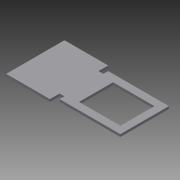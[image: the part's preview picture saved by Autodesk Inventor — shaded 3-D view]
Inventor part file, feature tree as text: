
AUTODESK INVENTOR PART (.ipt)
format: ipt  version: 2014 (Build 180170000, 170)  size: 101,376 bytes
history: native  units: mm
features: extrude x2, sketch x2
ambient origin geometry x8: Origin, YZ Plane, XZ Plane, XY Plane, X Axis, Y Axis, Z Axis, Center Point
bodies: Volumenkörper1 (feature_tree)
feature tree (4):
  extrude  "Extrusion1"  Depth=2.4mm
  extrude  "Extrusion2"  Depth=0.2mm
  sketch  "Skizze1"  dims[d0=4.5mm d1=2.4mm]
  sketch  "Skizze2"  dims[d4=2.5mm d5=0.2mm d6=0.2mm d7=0.2mm d8=0.2mm d9=0.4mm d10=0.4mm d11=0.1mm d12=0.0mm d13=0.3mm d14=0.3mm d15=0.3mm d16=0.5mm d17=0.1mm d18=0.0mm]
